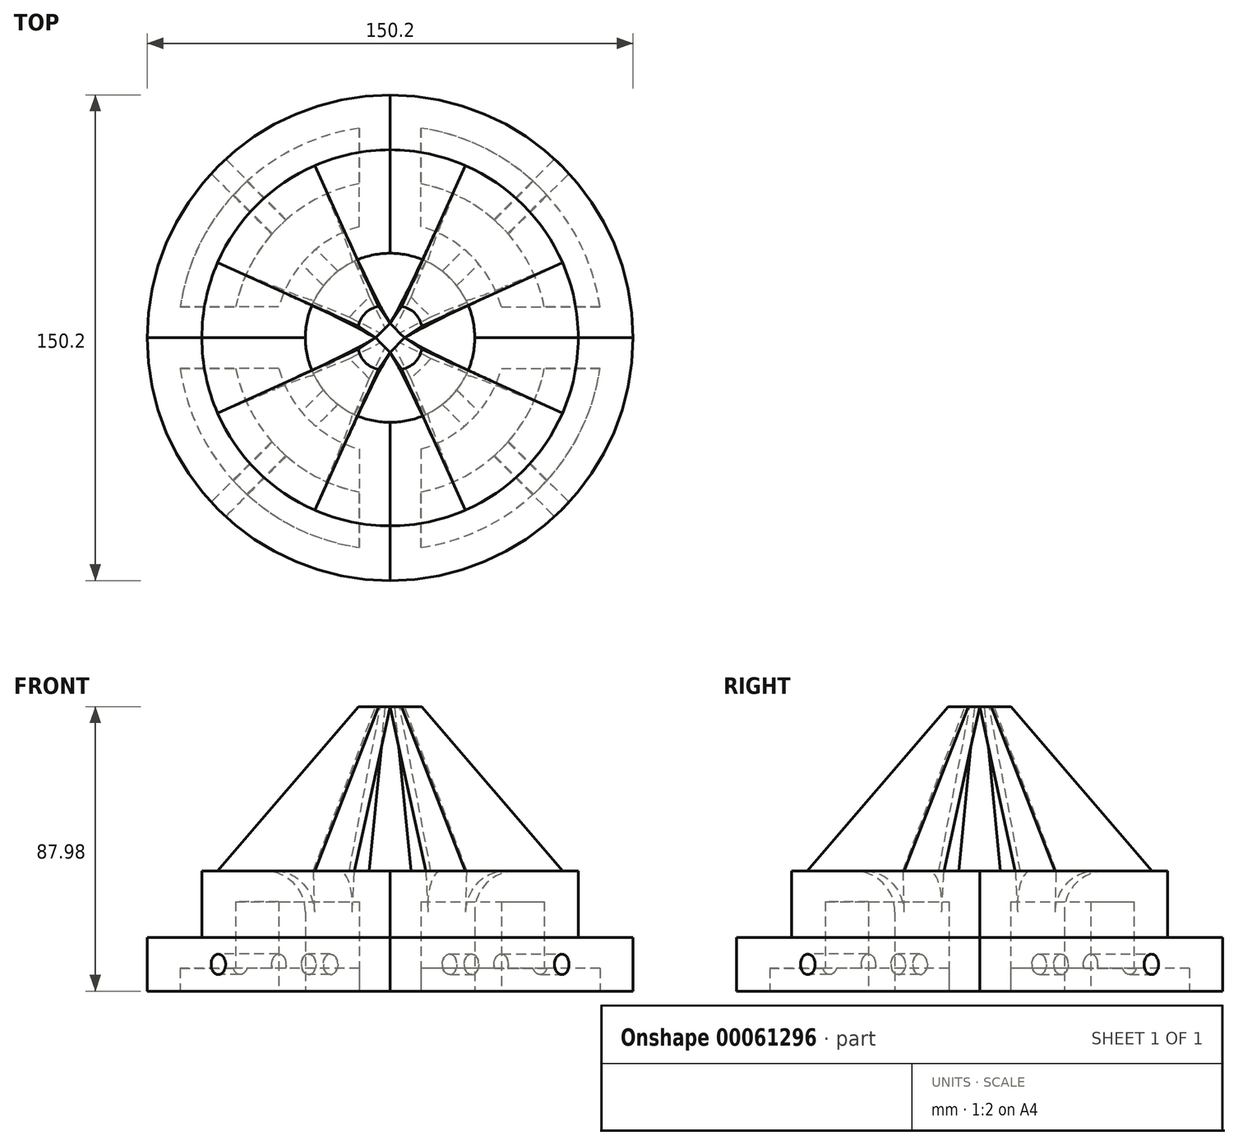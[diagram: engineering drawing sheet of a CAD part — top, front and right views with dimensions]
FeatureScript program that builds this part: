
annotation { "Feature Type Name" : "Feature", "Feature Type Description" : "" }
export const myFeature = defineFeature(function(context is Context, id is Id, definition is map)
    precondition{}
    {
        {
            var Q0;
            Q0=qCreatedBy(makeId("Right.planeOp"),FACE);
            var sketch = newSketch(context, id + "F0", { "sketchPlane" : qUnion([Q0])});
            skLineSegment(sketch, "E0", {"start": v(-75.1, 0) * mm, "end": v(-75.1, 16.54) * mm});
            skLineSegment(sketch, "E1", {"start": v(-75.1, 16.54) * mm, "end": v(-58.16, 16.54) * mm});
            skLineSegment(sketch, "E2", {"start": v(-58.16, 16.54) * mm, "end": v(-58.16, 37.18) * mm});
            skLineSegment(sketch, "E3", {"start": v(-26.17, 37.18) * mm, "end": v(-26.17, 0) * mm});
            skLineSegment(sketch, "E4", {"start": v(-26.17, 0) * mm, "end": v(-75.1, 0) * mm});
            skLineSegment(sketch, "E5", {"start": v(0, 0) * mm, "end": v(0, 84.17) * mm, "construction": true});
            skLineSegment(sketch, "E6", {"start": v(-26.17, 37.18) * mm, "end": v(-58.16, 37.18) * mm});
            skSolve(sketch);
        }
        {
            var Q0;
            Q0=makeQuery(id+"F0.imprint","IMPRINT",FACE,{"disambiguationData":[TD([[makeQuery(id+"F0.imprint","IMPRINT",EDGE,{"derivedFrom":sQuery(id+"F0.wireOp",EDGE,"E0")}),-1.0]])]});
            var Q1;
            Q1=sQuery(id+"F0.wireOp",EDGE,"E3");
            var Q2;
            Q2=sQuery(id+"F0.wireOp",EDGE,"98a4e65e-aeaa-49af-9cdd-b4144ff3290d");
            var Q3;
            Q3=sQuery(id+"F0.wireOp",EDGE,"E2");
            var Q4;
            Q4=sQuery(id+"F0.wireOp",EDGE,"E1");
            var Q5;
            Q5=sQuery(id+"F0.wireOp",EDGE,"E0");
            var Q6;
            Q6=sQuery(id+"F0.wireOp",EDGE,"E4");
            var Q7;
            Q7=sQuery(id+"F0.wireOp",EDGE,"E5");
            revolve(context, id + "F1", {"entities" : qUnion([Q0]), "surfaceEntities" : qUnion([Q1, Q2, Q3, Q4, Q5, Q6]), "axis" : qUnion([Q7]), "revolveType" : RevolveType.ONE_DIRECTION, "angle" : 90 * degree});
        }
        {
            var Q0;
            Q0=makeQuery(id+"F1.opRevolve","SWEPT_FACE",FACE,{"disambiguationData":[OSD([sQuery(id+"F0.wireOp",EDGE,"E4")])]});
            var Q1;
            Q1=makeQuery(id+"F1.opRevolve","SWEPT_BODY",BODY,{"disambiguationData":[OSD([sQuery(id+"F0.wireOp",EDGE,"E0"),sQuery(id+"F0.wireOp",EDGE,"E1"),sQuery(id+"F0.wireOp",EDGE,"E2"),sQuery(id+"F0.wireOp",EDGE,"E3"),sQuery(id+"F0.wireOp",EDGE,"E4"),sQuery(id+"F0.wireOp",EDGE,"E6")])]});
            shell(context, id + "F2", {"entities" : qUnion([Q0]), "parts" : qUnion([Q1]), "thickness" : 9.52 * mm});
        }
        {
            var Q0;
            Q0=makeQuery(id+"F1.opRevolve","SWEPT_FACE",FACE,{"disambiguationData":[OSD([sQuery(id+"F0.wireOp",EDGE,"E6")])]});
            var sketch = newSketch(context, id + "F3", { "sketchPlane" : qUnion([Q0])});
            skLineSegment(sketch, "E7", {"start": v(53.3, -23.28) * mm, "end": v(23.73, -11.03) * mm});
            skArc(sketch, "E8.0", {"start": v(23.73, -11.03) * mm, "mid": v(18.5, -18.5) * mm, "end": v(11.03, -23.73) * mm});
            skArc(sketch, "E9.0", {"start": v(53.3, -23.28) * mm, "mid": v(41.12, -41.12) * mm, "end": v(23.28, -53.3) * mm});
            skPoint(sketch, "E10.orphan", {"position": v(0, -58.16) * mm});
            skPoint(sketch, "E11.orphan", {"position": v(0, -26.17) * mm});
            skPoint(sketch, "E12.orphan", {"position": v(26.17, 0) * mm});
            skPoint(sketch, "E13.orphan", {"position": v(58.16, 0) * mm});
            skLineSegment(sketch, "E14", {"start": v(23.28, -53.3) * mm, "end": v(11.03, -23.73) * mm});
            skPoint(sketch, "E15", {"position": v(18.5, -18.5) * mm});
            skLineSegment(sketch, "E16", {"start": v(11.03, -23.73) * mm, "end": v(6.43, -12.62) * mm});
            skLineSegment(sketch, "E17", {"start": v(23.73, -11.03) * mm, "end": v(12.62, -6.43) * mm});
            skLineSegment(sketch, "E18", {"start": v(12.62, -6.43) * mm, "end": v(6.43, -12.62) * mm});
            skLineSegment(sketch, "E19", {"start": v(6.43, -12.62) * mm, "end": v(0, -12.62) * mm, "construction": true});
            skLineSegment(sketch, "E20", {"start": v(12.62, 0) * mm, "end": v(12.62, -6.43) * mm, "construction": true});
            skSolve(sketch);
        }
        {
            var Q0;
            Q0=makeQuery(id+"F3.imprint","IMPRINT",FACE,{"disambiguationData":[TD([[makeQuery(id+"F3.imprint","IMPRINT",EDGE,{"derivedFrom":sQuery(id+"F3.wireOp",EDGE,"E7")}),1.0]])]});
            cPlane(context, id + "F4", {"entities" : qUnion([Q0]), "cplaneType" : CPlaneType.OFFSET, "offset" : 50.8 * mm, "width" : 152.4 * mm, "height" : 152.4 * mm});
        }
        {
            var Q0;
            Q0=qCreatedBy(id+"F4.planeOp",FACE);
            var sketch = newSketch(context, id + "F5", { "sketchPlane" : qUnion([Q0])});
            skLineSegment(sketch, "E21", {"start": v(4.5, 0) * mm, "end": v(0, -4.5) * mm});
            skLineSegment(sketch, "E22", {"start": v(0, -4.5) * mm, "end": v(3.56, -9.75) * mm});
            skArc(sketch, "E23", {"start": v(3.56, -9.75) * mm, "mid": v(7.63, -7.63) * mm, "end": v(9.75, -3.56) * mm});
            skLineSegment(sketch, "E24", {"start": v(9.75, -3.56) * mm, "end": v(4.5, 0) * mm});
            skLineSegment(sketch, "E25", {"start": v(0, -4.5) * mm, "end": v(0, 0) * mm, "construction": true});
            skLineSegment(sketch, "E26", {"start": v(0, 0) * mm, "end": v(4.5, 0) * mm, "construction": true});
            skSolve(sketch);
        }
        {
            var Q1;
            Q1 = qSketchRegion(id + "F3", true);
            var Q2;
            Q2 = qSketchRegion(id + "F5", true);
            loft(context, id + "F6", {"operationType" : NewBodyOperationType.ADD, "sheetProfilesArray" : [{ "sheetProfileEntities" : qUnion([Q1]) }, { "sheetProfileEntities" : qUnion([Q2]) }]});
        }
        {
            var Q0;
            Q0=qCreatedBy(makeId("Front.planeOp"),FACE);
            var sketch = newSketch(context, id + "F7", { "sketchPlane" : qUnion([Q0])});
            skLineSegment(sketch, "E27", {"start": v(0, 0) * mm, "end": v(0, 101.26) * mm, "construction": true});
            skSolve(sketch);
        }
        {
            var Q0;
            {var subQ0=sQuery(id+"F5.wireOp",EDGE,"7e04f4c2-8fb7-4243-b27f-478c8cb61137");var subQ1=sQuery(id+"F5.wireOp",EDGE,"acb221f3-b319-4b66-9059-0958f30913aa");var subQ2=sQuery(id+"F3.wireOp",EDGE,"E16");var subQ3=sQuery(id+"F3.wireOp",EDGE,"861f3250-b69a-430a-9e5d-38a851b1d96f.0");var subQ4=sQuery(id+"F3.wireOp",EDGE,"E14");var subQ5=sQuery(id+"F3.wireOp",EDGE,"E9.0");var subQ6=sQuery(id+"F0.wireOp",EDGE,"E6");var subQ7=sQuery(id+"F0.wireOp",EDGE,"E2");var subQ8=sQuery(id+"F3.wireOp",EDGE,"E17");var subQ9=sQuery(id+"F3.wireOp",EDGE,"E7");var subQ10=sQuery(id+"F0.wireOp",EDGE,"E3");var subQ11=makeQuery(id+"F3.imprint","IMPRINT",EDGE,{"derivedFrom":sQuery(id+"F3.wireOp",EDGE,"E8.0")});Q0=makeQuery(id+"F6.boolean.opBoolean","SPLIT",EDGE,{"disambiguationData":[TD([makeQuery(id+"F1.opRevolve","SWEPT_FACE",FACE,{"disambiguationData":[OSD([subQ10])]}),makeQuery(id+"F1.opRevolve","SWEPT_FACE",FACE,{"disambiguationData":[OSD([subQ6])]}),makeQuery(id+"F6.opLoft","SWEPT_FACE",FACE,{"disambiguationData":[OSD([subQ7,subQ6,subQ9,subQ5,subQ3,subQ8,sQuery(id+"F5.wireOp",EDGE,"Cu43ddvo-ng6Z-f3fH-Borm-I5GrP3YaGcei"),subQ1,subQ0])]}),makeQuery(id+"F6.opLoft","SWEPT_FACE",FACE,{"disambiguationData":[OSD([subQ7,subQ6,subQ5,subQ4,subQ3,subQ2,sQuery(id+"F5.wireOp",EDGE,"MNGc9qBW-LTLU-AJqV-Pgwf-4KyOUYKcS0TR"),subQ1,subQ0])]}),makeQuery(id+"F6.opLoft","CAP_FACE",FACE,{"disambiguationData":[OSD([makeQuery(id+"F3.imprint","IMPRINT",FACE,{"disambiguationData":[TD([[subQ11,-1.0]])]}),makeQuery(id+"F3.imprint","IMPRINT",FACE,{"disambiguationData":[TD([[makeQuery(id+"F3.imprint","IMPRINT",EDGE,{"derivedFrom":subQ9}),1.0]])]})])],"isStart":true})])],"derivedFrom":makeQuery(id+"F1.opRevolve","SWEPT_EDGE",EDGE,{"disambiguationData":[OSD([subQ10,subQ6])]})});}
            var Q1;
            {var subQ0=sQuery(id+"F5.wireOp",EDGE,"7e04f4c2-8fb7-4243-b27f-478c8cb61137");var subQ1=sQuery(id+"F5.wireOp",EDGE,"acb221f3-b319-4b66-9059-0958f30913aa");var subQ2=sQuery(id+"F3.wireOp",EDGE,"E16");var subQ3=sQuery(id+"F3.wireOp",EDGE,"861f3250-b69a-430a-9e5d-38a851b1d96f.0");var subQ4=sQuery(id+"F3.wireOp",EDGE,"E14");var subQ5=sQuery(id+"F3.wireOp",EDGE,"E9.0");var subQ6=sQuery(id+"F0.wireOp",EDGE,"E6");var subQ7=sQuery(id+"F0.wireOp",EDGE,"E2");var subQ8=sQuery(id+"F3.wireOp",EDGE,"E17");var subQ9=sQuery(id+"F3.wireOp",EDGE,"E7");var subQ10=sQuery(id+"F0.wireOp",EDGE,"E3");var subQ11=makeQuery(id+"F3.imprint","IMPRINT",EDGE,{"derivedFrom":sQuery(id+"F3.wireOp",EDGE,"E8.0")});Q1=makeQuery(id+"F13.opPattern","COPY",EDGE,{"derivedFrom":makeQuery(id+"F6.boolean.opBoolean","SPLIT",EDGE,{"disambiguationData":[TD([makeQuery(id+"F1.opRevolve","SWEPT_FACE",FACE,{"disambiguationData":[OSD([subQ10])]}),makeQuery(id+"F1.opRevolve","SWEPT_FACE",FACE,{"disambiguationData":[OSD([subQ6])]}),makeQuery(id+"F6.opLoft","SWEPT_FACE",FACE,{"disambiguationData":[OSD([subQ7,subQ6,subQ9,subQ5,subQ3,subQ8,sQuery(id+"F5.wireOp",EDGE,"Cu43ddvo-ng6Z-f3fH-Borm-I5GrP3YaGcei"),subQ1,subQ0])]}),makeQuery(id+"F6.opLoft","SWEPT_FACE",FACE,{"disambiguationData":[OSD([subQ7,subQ6,subQ5,subQ4,subQ3,subQ2,sQuery(id+"F5.wireOp",EDGE,"MNGc9qBW-LTLU-AJqV-Pgwf-4KyOUYKcS0TR"),subQ1,subQ0])]}),makeQuery(id+"F6.opLoft","CAP_FACE",FACE,{"disambiguationData":[OSD([makeQuery(id+"F3.imprint","IMPRINT",FACE,{"disambiguationData":[TD([[subQ11,-1.0]])]}),makeQuery(id+"F3.imprint","IMPRINT",FACE,{"disambiguationData":[TD([[makeQuery(id+"F3.imprint","IMPRINT",EDGE,{"derivedFrom":subQ9}),1.0]])]})])],"isStart":true})])],"derivedFrom":makeQuery(id+"F1.opRevolve","SWEPT_EDGE",EDGE,{"disambiguationData":[OSD([subQ10,subQ6])]})}),"instanceName":"1"});}
            var Q2;
            {var subQ0=sQuery(id+"F5.wireOp",EDGE,"7e04f4c2-8fb7-4243-b27f-478c8cb61137");var subQ1=sQuery(id+"F5.wireOp",EDGE,"acb221f3-b319-4b66-9059-0958f30913aa");var subQ2=sQuery(id+"F3.wireOp",EDGE,"E16");var subQ3=sQuery(id+"F3.wireOp",EDGE,"861f3250-b69a-430a-9e5d-38a851b1d96f.0");var subQ4=sQuery(id+"F3.wireOp",EDGE,"E14");var subQ5=sQuery(id+"F3.wireOp",EDGE,"E9.0");var subQ6=sQuery(id+"F0.wireOp",EDGE,"E6");var subQ7=sQuery(id+"F0.wireOp",EDGE,"E2");var subQ8=sQuery(id+"F3.wireOp",EDGE,"E17");var subQ9=sQuery(id+"F3.wireOp",EDGE,"E7");var subQ10=sQuery(id+"F0.wireOp",EDGE,"E3");var subQ11=makeQuery(id+"F3.imprint","IMPRINT",EDGE,{"derivedFrom":sQuery(id+"F3.wireOp",EDGE,"E8.0")});Q2=makeQuery(id+"F13.opPattern","COPY",EDGE,{"derivedFrom":makeQuery(id+"F6.boolean.opBoolean","SPLIT",EDGE,{"disambiguationData":[TD([makeQuery(id+"F1.opRevolve","SWEPT_FACE",FACE,{"disambiguationData":[OSD([subQ10])]}),makeQuery(id+"F1.opRevolve","SWEPT_FACE",FACE,{"disambiguationData":[OSD([subQ6])]}),makeQuery(id+"F6.opLoft","SWEPT_FACE",FACE,{"disambiguationData":[OSD([subQ7,subQ6,subQ9,subQ5,subQ3,subQ8,sQuery(id+"F5.wireOp",EDGE,"Cu43ddvo-ng6Z-f3fH-Borm-I5GrP3YaGcei"),subQ1,subQ0])]}),makeQuery(id+"F6.opLoft","SWEPT_FACE",FACE,{"disambiguationData":[OSD([subQ7,subQ6,subQ5,subQ4,subQ3,subQ2,sQuery(id+"F5.wireOp",EDGE,"MNGc9qBW-LTLU-AJqV-Pgwf-4KyOUYKcS0TR"),subQ1,subQ0])]}),makeQuery(id+"F6.opLoft","CAP_FACE",FACE,{"disambiguationData":[OSD([makeQuery(id+"F3.imprint","IMPRINT",FACE,{"disambiguationData":[TD([[subQ11,-1.0]])]}),makeQuery(id+"F3.imprint","IMPRINT",FACE,{"disambiguationData":[TD([[makeQuery(id+"F3.imprint","IMPRINT",EDGE,{"derivedFrom":subQ9}),1.0]])]})])],"isStart":true})])],"derivedFrom":makeQuery(id+"F1.opRevolve","SWEPT_EDGE",EDGE,{"disambiguationData":[OSD([subQ10,subQ6])]})}),"instanceName":"2"});}
            var Q3;
            {var subQ0=sQuery(id+"F5.wireOp",EDGE,"7e04f4c2-8fb7-4243-b27f-478c8cb61137");var subQ1=sQuery(id+"F5.wireOp",EDGE,"acb221f3-b319-4b66-9059-0958f30913aa");var subQ2=sQuery(id+"F3.wireOp",EDGE,"E16");var subQ3=sQuery(id+"F3.wireOp",EDGE,"861f3250-b69a-430a-9e5d-38a851b1d96f.0");var subQ4=sQuery(id+"F3.wireOp",EDGE,"E14");var subQ5=sQuery(id+"F3.wireOp",EDGE,"E9.0");var subQ6=sQuery(id+"F0.wireOp",EDGE,"E6");var subQ7=sQuery(id+"F0.wireOp",EDGE,"E2");var subQ8=sQuery(id+"F3.wireOp",EDGE,"E17");var subQ9=sQuery(id+"F3.wireOp",EDGE,"E7");var subQ10=sQuery(id+"F0.wireOp",EDGE,"E3");var subQ11=makeQuery(id+"F3.imprint","IMPRINT",EDGE,{"derivedFrom":sQuery(id+"F3.wireOp",EDGE,"E8.0")});Q3=makeQuery(id+"F13.opPattern","COPY",EDGE,{"derivedFrom":makeQuery(id+"F6.boolean.opBoolean","SPLIT",EDGE,{"disambiguationData":[TD([makeQuery(id+"F1.opRevolve","SWEPT_FACE",FACE,{"disambiguationData":[OSD([subQ10])]}),makeQuery(id+"F1.opRevolve","SWEPT_FACE",FACE,{"disambiguationData":[OSD([subQ6])]}),makeQuery(id+"F6.opLoft","SWEPT_FACE",FACE,{"disambiguationData":[OSD([subQ7,subQ6,subQ9,subQ5,subQ3,subQ8,sQuery(id+"F5.wireOp",EDGE,"Cu43ddvo-ng6Z-f3fH-Borm-I5GrP3YaGcei"),subQ1,subQ0])]}),makeQuery(id+"F6.opLoft","SWEPT_FACE",FACE,{"disambiguationData":[OSD([subQ7,subQ6,subQ5,subQ4,subQ3,subQ2,sQuery(id+"F5.wireOp",EDGE,"MNGc9qBW-LTLU-AJqV-Pgwf-4KyOUYKcS0TR"),subQ1,subQ0])]}),makeQuery(id+"F6.opLoft","CAP_FACE",FACE,{"disambiguationData":[OSD([makeQuery(id+"F3.imprint","IMPRINT",FACE,{"disambiguationData":[TD([[subQ11,-1.0]])]}),makeQuery(id+"F3.imprint","IMPRINT",FACE,{"disambiguationData":[TD([[makeQuery(id+"F3.imprint","IMPRINT",EDGE,{"derivedFrom":subQ9}),1.0]])]})])],"isStart":true})])],"derivedFrom":makeQuery(id+"F1.opRevolve","SWEPT_EDGE",EDGE,{"disambiguationData":[OSD([subQ10,subQ6])]})}),"instanceName":"3"});}
            fillet(context, id + "F8", {"entities" : qUnion([Q0, Q1, Q2, Q3]), "radius" : 12.7 * mm, "tangentPropagation" : true, "allowEdgeOverflow" : false});
        }
        {
            var Q0;
            Q0=makeQuery(id+"F1.opRevolve","SWEPT_FACE",FACE,{"disambiguationData":[OSD([sQuery(id+"F0.wireOp",EDGE,"E1")])]});
            var sketch = newSketch(context, id + "F9", { "sketchPlane" : qUnion([Q0])});
            skLineSegment(sketch, "E28", {"start": v(0, 0) * mm, "end": v(53.1, -53.1) * mm, "construction": true});
            skSolve(sketch);
        }
        {
            var Q0;
            Q0=sQuery(id+"F9.wireOp",EDGE,"E28");
            var Q1;
            Q1=sQuery(id+"F9.wireOp",VERTEX,"E28.end");
            cPlane(context, id + "F10", {"entities" : qUnion([Q0, Q1]), "cplaneType" : CPlaneType.LINE_POINT, "offset" : 152.4 * mm, "width" : 152.4 * mm, "height" : 152.4 * mm});
        }
        {
            var Q0;
            Q0=qCreatedBy(id+"F10.planeOp",FACE);
            var sketch = newSketch(context, id + "F11", { "sketchPlane" : qUnion([Q0])});
            skPoint(sketch, "E29", {"position": v(0, 8.27) * mm});
            skLineSegment(sketch, "E30", {"start": v(0, 0) * mm, "end": v(0, 16.54) * mm, "construction": true});
            skCircle(sketch, "E31", {"center": v(0, 8.27) * mm, "radius": 3.18 * mm});
            skSolve(sketch);
        }
        {
            var Q0;
            Q0 = qSketchRegion(id + "F11", true);
            extrude(context, id + "F12", {"entities" : qUnion([Q0]), "operationType" : NewBodyOperationType.REMOVE, "endBound" : BoundingType.THROUGH_ALL, "oppositeDirection" : true, "depth" : 25.4 * mm});
        }
        {
            var Q0;
            Q0=makeQuery(id+"F1.opRevolve","SWEPT_BODY",BODY,{"disambiguationData":[OSD([sQuery(id+"F0.wireOp",EDGE,"E0"),sQuery(id+"F0.wireOp",EDGE,"E1"),sQuery(id+"F0.wireOp",EDGE,"E2"),sQuery(id+"F0.wireOp",EDGE,"E3"),sQuery(id+"F0.wireOp",EDGE,"E4"),sQuery(id+"F0.wireOp",EDGE,"E6")])]});
            var Q1;
            Q1=sQuery(id+"F7.wireOp",EDGE,"E27");
            circularPattern(context, id + "F13", {"entities" : qUnion([Q0]), "axis" : qUnion([Q1]), "angle" : 360 * degree, "instanceCount" : 4, "equalSpace" : true});
        }
    });
